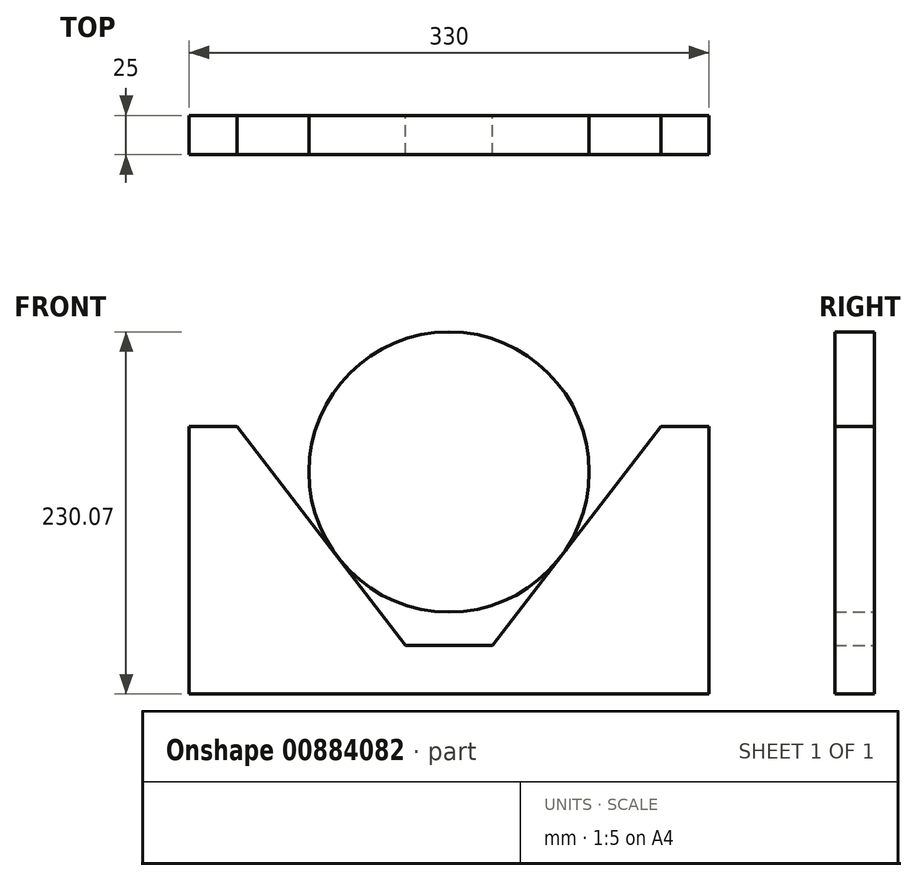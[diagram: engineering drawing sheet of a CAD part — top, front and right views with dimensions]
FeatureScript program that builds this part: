
annotation { "Feature Type Name" : "Feature", "Feature Type Description" : "" }
export const myFeature = defineFeature(function(context is Context, id is Id, definition is map)
    precondition{}
    {
        {
            var Q0;
            Q0=qCreatedBy(makeId("Front.planeOp"),FACE);
            var sketch = newSketch(context, id + "F0", { "sketchPlane" : qUnion([Q0])});
            skCircle(sketch, "E0", {"center": v(0, 0) * mm, "radius": 89 * mm});
            skSolve(sketch);
        }
        {
            var Q0;
            Q0=qCreatedBy(makeId("Front.planeOp"),FACE);
            var sketch = newSketch(context, id + "F1", { "sketchPlane" : qUnion([Q0])});
            skLineSegment(sketch, "E1", {"start": v(27.64, -110) * mm, "end": v(134.58, 28.93) * mm});
            skLineSegment(sketch, "E2", {"start": v(134.58, 28.93) * mm, "end": v(165, 28.93) * mm});
            skLineSegment(sketch, "E3", {"start": v(165, 28.93) * mm, "end": v(165, -141.07) * mm});
            skLineSegment(sketch, "E4", {"start": v(165, -141.07) * mm, "end": v(-27.95, -141.07) * mm});
            skLineSegment(sketch, "E5", {"start": v(0, -110) * mm, "end": v(27.64, -110) * mm});
            skPoint(sketch, "E6.start.orphan", {"position": v(0, 0) * mm});
            skLineSegment(sketch, "E7.MirrorCS", {"start": v(-27.64, -110) * mm, "end": v(-134.58, 28.93) * mm});
            skLineSegment(sketch, "E8.MirrorCS", {"start": v(-134.58, 28.93) * mm, "end": v(-165, 28.93) * mm});
            skLineSegment(sketch, "E9.MirrorCS", {"start": v(-165, 28.93) * mm, "end": v(-165, -141.07) * mm});
            skLineSegment(sketch, "E10.MirrorCS", {"start": v(-165, -141.07) * mm, "end": v(27.95, -141.07) * mm});
            skLineSegment(sketch, "E11.MirrorCS", {"start": v(0, -110) * mm, "end": v(-27.64, -110) * mm});
            skPoint(sketch, "E12.MirrorCS.end.orphan", {"position": v(0, -140) * mm});
            skPoint(sketch, "E12.MirrorCS.start.orphan", {"position": v(0, -110) * mm});
            skSolve(sketch);
        }
        {
            var Q0;
            Q0=makeQuery(id+"F1.imprint","IMPRINT",FACE,{"disambiguationData":[TD([[makeQuery(id+"F1.imprint","IMPRINT",EDGE,{"derivedFrom":sQuery(id+"F1.wireOp",EDGE,"E1")}),-1.0]])]});
            extrude(context, id + "F2", {"entities" : qUnion([Q0]), "depth" : 25 * mm, "offsetDistance" : 25 * mm});
        }
        {
            var Q0;
            Q0=makeQuery(id+"F0.imprint","IMPRINT",FACE,{"disambiguationData":[TD([[makeQuery(id+"F0.imprint","IMPRINT",EDGE,{"derivedFrom":sQuery(id+"F0.wireOp",EDGE,"E0")}),1.0]])]});
            extrude(context, id + "F3", {"entities" : qUnion([Q0]), "operationType" : NewBodyOperationType.ADD, "depth" : 25 * mm, "offsetDistance" : 25 * mm});
        }
    });
